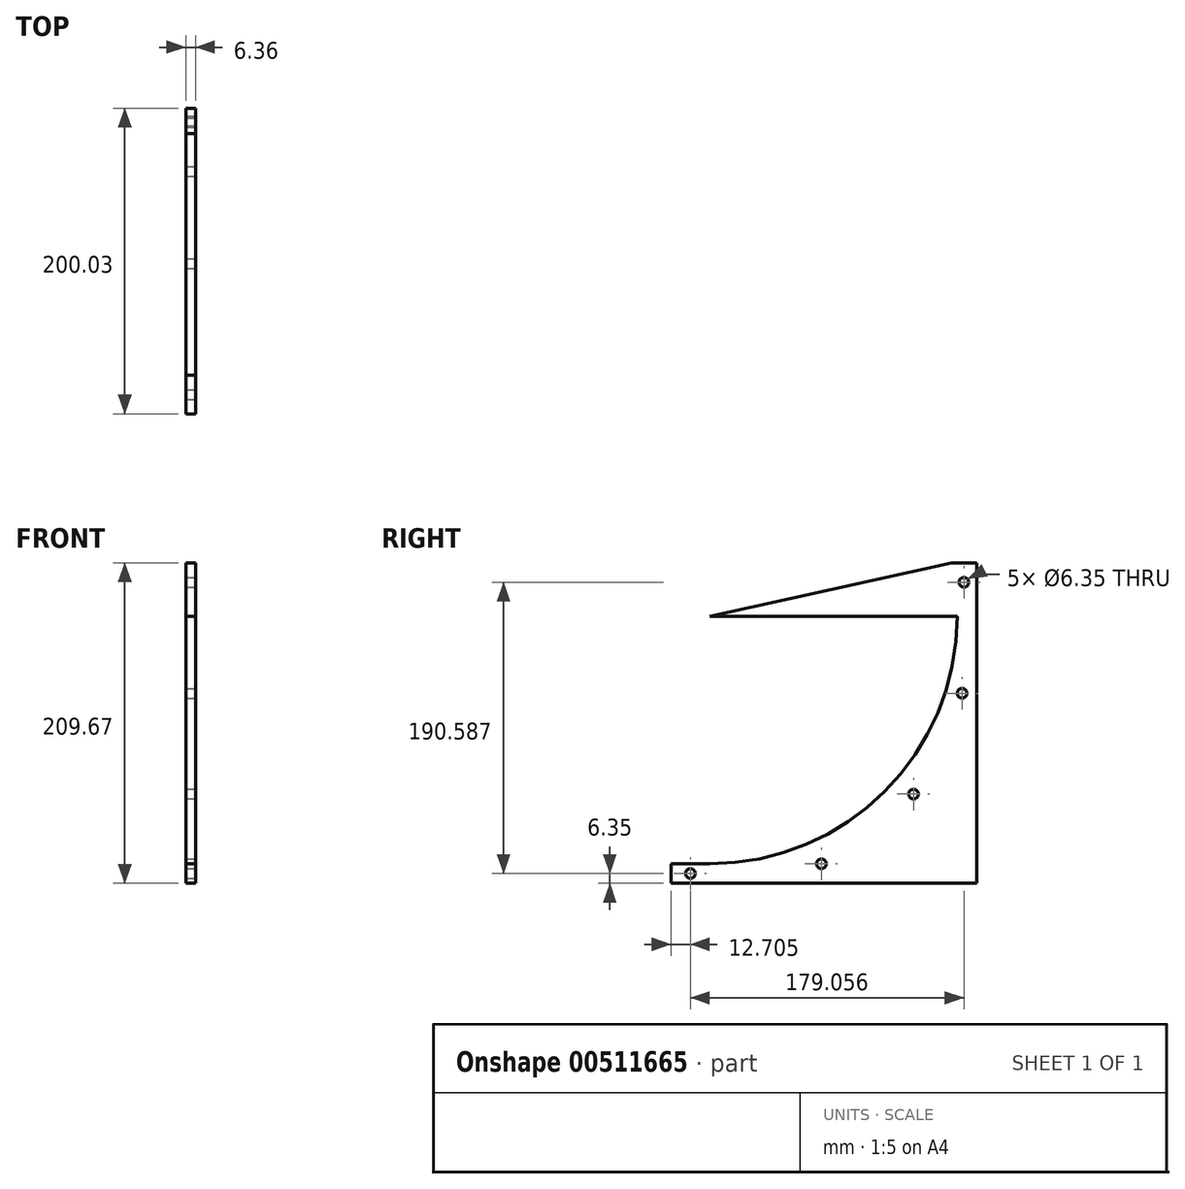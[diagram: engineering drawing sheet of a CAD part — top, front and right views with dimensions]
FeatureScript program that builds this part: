
annotation { "Feature Type Name" : "Feature", "Feature Type Description" : "" }
export const myFeature = defineFeature(function(context is Context, id is Id, definition is map)
    precondition{}
    {
        {
            var Q0;
            Q0=qCreatedBy(makeId("Front.planeOp"),FACE);
            var sketch = newSketch(context, id + "F0", { "sketchPlane" : qUnion([Q0])});
            skLineSegment(sketch, "E0.bottom", {"start": v(-3.17, 127) * mm, "end": v(3.18, 127) * mm});
            skLineSegment(sketch, "E0.top", {"start": v(-3.18, -127) * mm, "end": v(3.17, -127) * mm});
            skLineSegment(sketch, "E0.left", {"start": v(-3.17, 127) * mm, "end": v(-3.18, -127) * mm});
            skLineSegment(sketch, "E0.right", {"start": v(3.18, 127) * mm, "end": v(3.17, -127) * mm});
            skPoint(sketch, "E0.middle", {"position": v(0, 0) * mm});
            skSolve(sketch);
        }
        {
            var Q0;
            Q0=makeQuery(id+"F0.imprint","IMPRINT",FACE,{"disambiguationData":[TD([[makeQuery(id+"F0.imprint","IMPRINT",EDGE,{"derivedFrom":sQuery(id+"F0.wireOp",EDGE,"E0.bottom")}),-1.0]])]});
            extrude(context, id + "F1", {"entities" : qUnion([Q0]), "depth" : 279.4 * mm, "offsetDistance" : 25.4 * mm});
        }
        {
            var Q0;
            Q0=makeQuery(id+"F1.opExtrude","SWEPT_FACE",FACE,{"disambiguationData":[OSD([sQuery(id+"F0.wireOp",EDGE,"E0.left")])]});
            var sketch = newSketch(context, id + "F2", { "sketchPlane" : qUnion([Q0])});
            skArc(sketch, "E1", {"start": v(16.54, 82.67) * mm, "mid": v(48.34, -53.73) * mm, "end": v(174.63, -114.3) * mm});
            skLineSegment(sketch, "E2.0.0", {"start": v(0, 82.67) * mm, "end": v(0, -127) * mm});
            skLineSegment(sketch, "E2.0.1", {"start": v(0, -127) * mm, "end": v(279.4, -127) * mm});
            skLineSegment(sketch, "E2.0.2", {"start": v(279.4, -127) * mm, "end": v(279.4, 127) * mm});
            skLineSegment(sketch, "E3", {"start": v(174.63, -114.3) * mm, "end": v(279.4, -114.3) * mm});
            skLineSegment(sketch, "E4", {"start": v(0, 82.67) * mm, "end": v(16.54, 82.67) * mm});
            skLineSegment(sketch, "E5", {"start": v(174.62, 47.63) * mm, "end": v(16.54, 82.67) * mm});
            skLineSegment(sketch, "E6", {"start": v(16.54, 82.67) * mm, "end": v(174.62, 47.63) * mm});
            skLineSegment(sketch, "E7", {"start": v(174.62, 47.63) * mm, "end": v(0, 47.62) * mm});
            skPoint(sketch, "E2.0.3.end.orphan", {"position": v(0, 127) * mm});
            skSolve(sketch);
        }
        {
            var Q0;
            {var subQ1=sQuery(id+"F2.wireOp",EDGE,"E3");Q0=makeQuery(id+"F2.imprint","IMPRINT",FACE,{"disambiguationData":[TD([[makeQuery(id+"F2.imprint","IMPRINT",EDGE,{"derivedFrom":subQ1}),1.0]])]});}
            var Q1;
            {var subQ0=sQuery(id+"F2.wireOp",EDGE,"E6");Q1=makeQuery(id+"F2.imprint","IMPRINT",FACE,{"disambiguationData":[TD([[makeQuery(id+"F2.imprint","IMPRINT",EDGE,{"derivedFrom":subQ0}),-1.0]])]});}
            extrude(context, id + "F3", {"entities" : qUnion([Q0, Q1]), "operationType" : NewBodyOperationType.REMOVE, "oppositeDirection" : true, "depth" : 25.4 * mm, "offsetDistance" : 25.4 * mm});
        }
        {
            var Q0;
            Q0=makeQuery(id+"F1.opExtrude","SWEPT_FACE",FACE,{"disambiguationData":[OSD([sQuery(id+"F0.wireOp",EDGE,"E0.left")])]});
            var sketch = newSketch(context, id + "F4", { "sketchPlane" : qUnion([Q0])});
            skLineSegment(sketch, "E8.0", {"start": v(174.63, -114.3) * mm, "end": v(279.4, -114.3) * mm});
            skLineSegment(sketch, "E9", {"start": v(200.03, -114.3) * mm, "end": v(200.03, -127) * mm});
            skLineSegment(sketch, "E10", {"start": v(200.03, -127) * mm, "end": v(279.4, -127) * mm});
            skLineSegment(sketch, "E11", {"start": v(279.4, -127) * mm, "end": v(279.4, -114.3) * mm});
            skSolve(sketch);
        }
        {
            var Q0;
            {var subQ2=sQuery(id+"F4.wireOp",EDGE,"E9");Q0=makeQuery(id+"F4.imprint","IMPRINT",FACE,{"disambiguationData":[TD([[makeQuery(id+"F4.imprint","IMPRINT",EDGE,{"derivedFrom":subQ2}),1.0]])]});}
            extrude(context, id + "F5", {"entities" : qUnion([Q0]), "operationType" : NewBodyOperationType.REMOVE, "oppositeDirection" : true, "depth" : 25.4 * mm, "offsetDistance" : 25.4 * mm});
        }
        {
            var Q0;
            Q0=makeQuery(id+"F1.opExtrude","SWEPT_FACE",FACE,{"disambiguationData":[OSD([sQuery(id+"F0.wireOp",EDGE,"E0.right")])]});
            var sketch = newSketch(context, id + "F6", { "sketchPlane" : qUnion([Q0])});
            skPoint(sketch, "E12", {"position": v(-187.33, -120.65) * mm});
            skPoint(sketch, "E12.positionSnap0", {"position": v(-200.03, -120.65) * mm});
            skPoint(sketch, "E13", {"position": v(-101.6, -114.3) * mm});
            skPoint(sketch, "E14", {"position": v(-41.28, -68.65) * mm});
            skPoint(sketch, "E15", {"position": v(-9.53, -2.67) * mm});
            skPoint(sketch, "E16", {"position": v(-8.27, 69.94) * mm});
            skPoint(sketch, "E16.positionSnap0", {"position": v(-8.27, 82.67) * mm});
            skSolve(sketch);
        }
        {
            var Q0;
            Q0=sQuery(id+"F6.wireOp",VERTEX,"E12");
            var Q1;
            Q1=sQuery(id+"F6.wireOp",VERTEX,"E13");
            var Q2;
            Q2=sQuery(id+"F6.wireOp",VERTEX,"E14");
            var Q3;
            Q3=sQuery(id+"F6.wireOp",VERTEX,"E15");
            var Q4;
            Q4=sQuery(id+"F6.wireOp",VERTEX,"E16");
            var Q5;
            Q5=makeQuery(id+"F1.opExtrude","SWEPT_BODY",BODY,{"disambiguationData":[OSD([sQuery(id+"F0.wireOp",EDGE,"E0.bottom"),sQuery(id+"F0.wireOp",EDGE,"E0.top"),sQuery(id+"F0.wireOp",EDGE,"E0.left"),sQuery(id+"F0.wireOp",EDGE,"E0.right")])]});
            hole(context, id + "F7", {"style" : HoleStyle.SIMPLE, "endStyle" : HoleEndStyle.THROUGH, "holeDiameter" : 6.35 * mm, "isTappedThrough" : true, "tappedDepth" : 12.7 * mm, "tapClearance" : 3, "locations" : qUnion([Q0, Q1, Q2, Q3, Q4]), "scope" : qUnion([Q5])});
        }
    });
